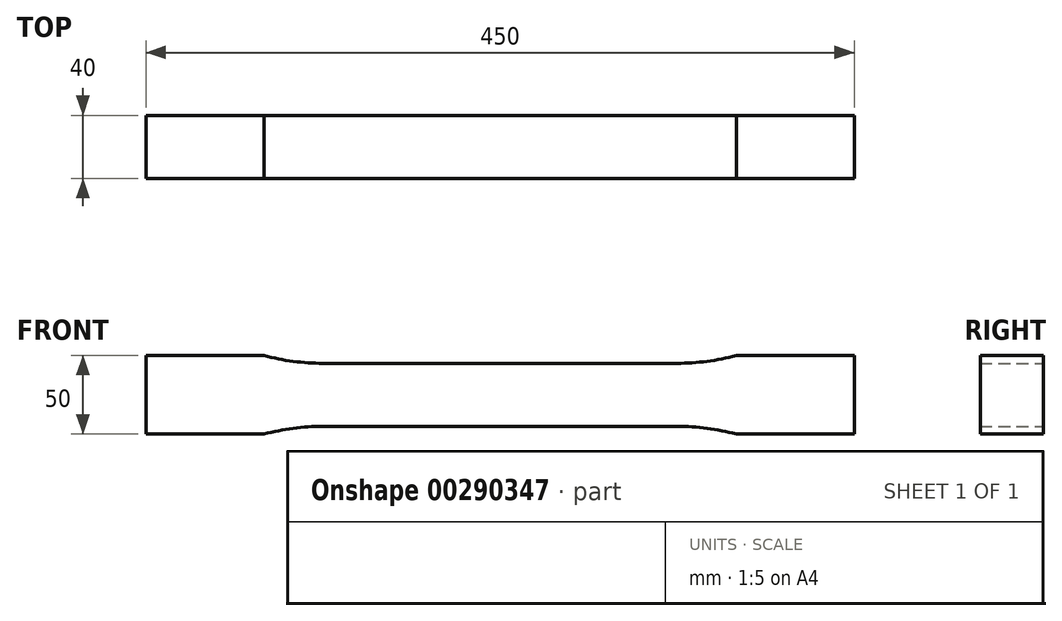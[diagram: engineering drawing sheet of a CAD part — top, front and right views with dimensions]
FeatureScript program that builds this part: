
annotation { "Feature Type Name" : "Feature", "Feature Type Description" : "" }
export const myFeature = defineFeature(function(context is Context, id is Id, definition is map)
    precondition{}
    {
        {
            var Q0;
            Q0=qCreatedBy(makeId("Front.planeOp"),FACE);
            var sketch = newSketch(context, id + "F0", { "sketchPlane" : qUnion([Q0])});
            skLineSegment(sketch, "E0", {"start": v(0, 20) * mm, "end": v(112.5, 20) * mm});
            skLineSegment(sketch, "E1", {"start": v(150, 25) * mm, "end": v(225, 25) * mm});
            skLineSegment(sketch, "E2", {"start": v(225, 25) * mm, "end": v(225, 0) * mm});
            skArc(sketch, "E3", {"start": v(112.5, 20) * mm, "mid": v(131.42, 21.26) * mm, "end": v(150, 25) * mm});
            skLineSegment(sketch, "E4.MirrorCS", {"start": v(150, -25) * mm, "end": v(225, -25) * mm});
            skArc(sketch, "E5.MirrorCS", {"start": v(112.5, -20) * mm, "mid": v(131.42, -21.26) * mm, "end": v(150, -25) * mm});
            skLineSegment(sketch, "E6.MirrorCS", {"start": v(0, -20) * mm, "end": v(112.5, -20) * mm});
            skLineSegment(sketch, "E7.MirrorCS", {"start": v(225, -25) * mm, "end": v(225, 0) * mm});
            skLineSegment(sketch, "E8.MirrorCS", {"start": v(-225, -25) * mm, "end": v(-225, 0) * mm});
            skLineSegment(sketch, "E9.MirrorCS", {"start": v(0, -20) * mm, "end": v(-112.5, -20) * mm});
            skLineSegment(sketch, "E10.MirrorCS", {"start": v(0, 20) * mm, "end": v(-112.5, 20) * mm});
            skLineSegment(sketch, "E11.MirrorCS", {"start": v(-150, 25) * mm, "end": v(-225, 25) * mm});
            skLineSegment(sketch, "E12.MirrorCS", {"start": v(-225, 25) * mm, "end": v(-225, 0) * mm});
            skArc(sketch, "E13.MirrorCS", {"start": v(-112.5, -20) * mm, "mid": v(-131.42, -21.26) * mm, "end": v(-150, -25) * mm});
            skLineSegment(sketch, "E14.MirrorCS", {"start": v(-150, -25) * mm, "end": v(-225, -25) * mm});
            skArc(sketch, "E15.MirrorCS", {"start": v(-112.5, 20) * mm, "mid": v(-131.42, 21.26) * mm, "end": v(-150, 25) * mm});
            skSolve(sketch);
        }
        {
            var Q0;
            Q0=makeQuery(id+"F0.imprint","IMPRINT",FACE,{"disambiguationData":[TD([[makeQuery(id+"F0.imprint","IMPRINT",EDGE,{"derivedFrom":sQuery(id+"F0.wireOp",EDGE,"E2")}),-1.0]])]});
            extrude(context, id + "F1", {"entities" : qUnion([Q0]), "depth" : 40 * mm});
        }
    });
